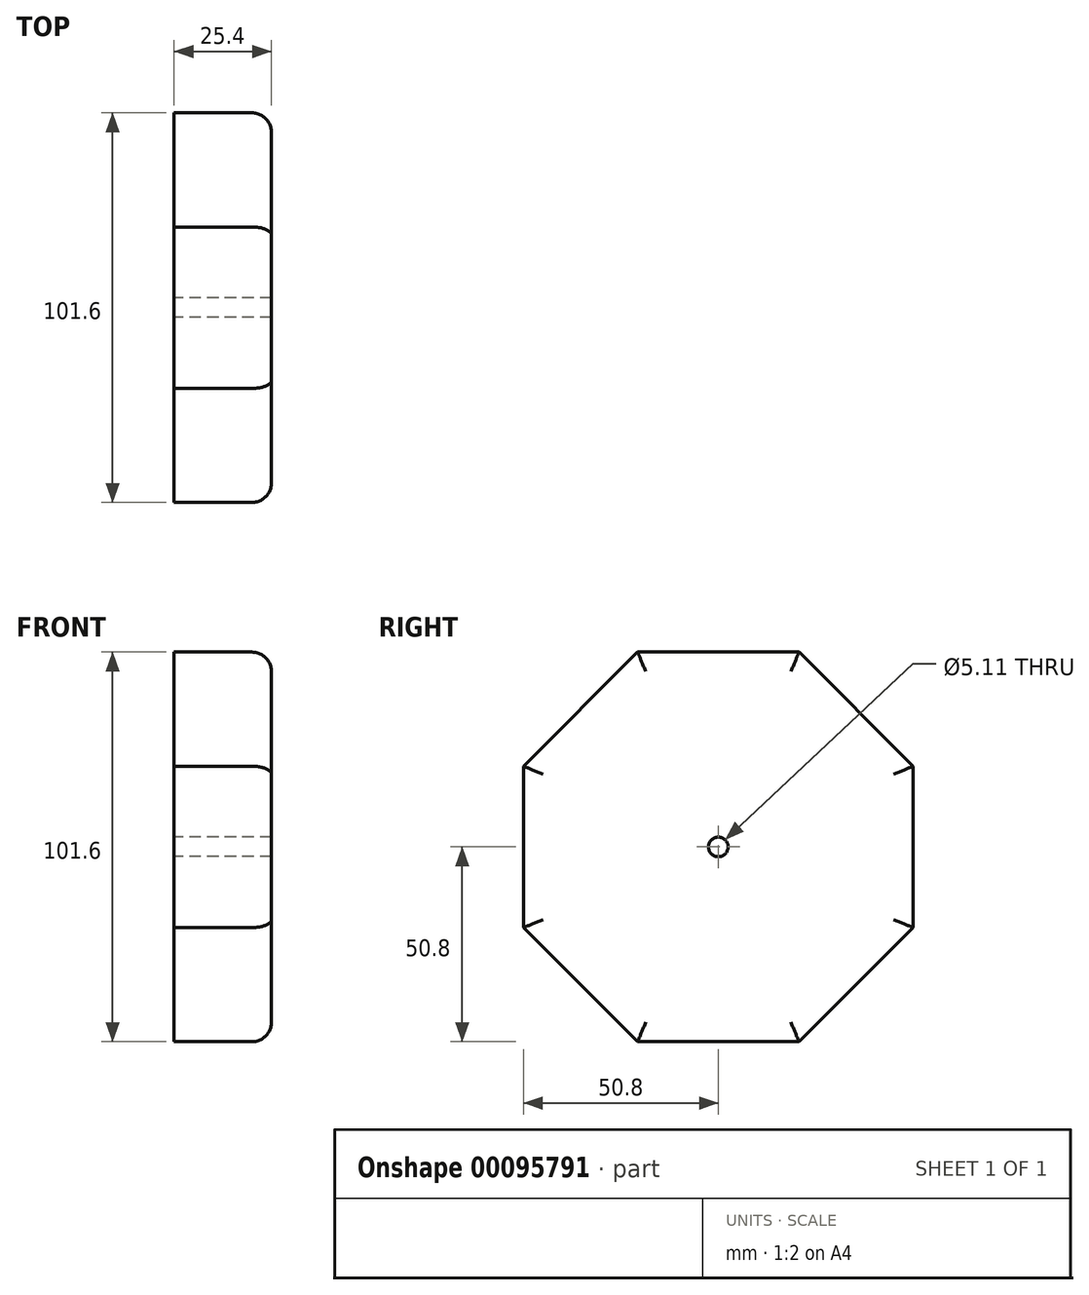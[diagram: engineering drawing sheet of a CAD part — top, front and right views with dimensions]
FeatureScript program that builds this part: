
annotation { "Feature Type Name" : "Feature", "Feature Type Description" : "" }
export const myFeature = defineFeature(function(context is Context, id is Id, definition is map)
    precondition{}
    {
        {
            var Q0;
            Q0=qCreatedBy(makeId("Right.planeOp"),FACE);
            var sketch = newSketch(context, id + "F0", { "sketchPlane" : qUnion([Q0])});
            skLineSegment(sketch, "E0.0", {"start": v(50.8, 21.04) * mm, "end": v(50.8, -21.04) * mm});
            skLineSegment(sketch, "E0.1", {"start": v(50.8, -21.04) * mm, "end": v(21.04, -50.8) * mm});
            skLineSegment(sketch, "E0.2", {"start": v(21.04, -50.8) * mm, "end": v(-21.04, -50.8) * mm});
            skLineSegment(sketch, "E0.3", {"start": v(-21.04, -50.8) * mm, "end": v(-50.8, -21.04) * mm});
            skLineSegment(sketch, "E0.4", {"start": v(-50.8, -21.04) * mm, "end": v(-50.8, 21.04) * mm});
            skLineSegment(sketch, "E0.5", {"start": v(-50.8, 21.04) * mm, "end": v(-21.04, 50.8) * mm});
            skLineSegment(sketch, "E0.6", {"start": v(-21.04, 50.8) * mm, "end": v(21.04, 50.8) * mm});
            skLineSegment(sketch, "E0.7", {"start": v(21.04, 50.8) * mm, "end": v(50.8, 21.04) * mm});
            skPoint(sketch, "E0.0.midPoint", {"position": v(50.8, 0) * mm});
            skPoint(sketch, "E1", {"position": v(0, 0) * mm});
            skSolve(sketch);
        }
        {
            var Q0;
            Q0 = qSketchRegion(id + "F0", true);
            extrude(context, id + "F1", {"entities" : qUnion([Q0]), "depth" : 25.4 * mm});
        }
        {
            var Q0;
            Q0=makeQuery(id+"F1.opExtrude","CAP_EDGE",EDGE,{"disambiguationData":[OSD([sQuery(id+"F0.wireOp",EDGE,"E0.5")])],"isStart":false});
            var Q1;
            Q1=makeQuery(id+"F1.opExtrude","CAP_EDGE",EDGE,{"disambiguationData":[OSD([sQuery(id+"F0.wireOp",EDGE,"E0.4")])],"isStart":false});
            var Q2;
            Q2=makeQuery(id+"F1.opExtrude","CAP_EDGE",EDGE,{"disambiguationData":[OSD([sQuery(id+"F0.wireOp",EDGE,"E0.3")])],"isStart":false});
            var Q3;
            Q3=makeQuery(id+"F1.opExtrude","CAP_EDGE",EDGE,{"disambiguationData":[OSD([sQuery(id+"F0.wireOp",EDGE,"E0.2")])],"isStart":false});
            var Q4;
            Q4=makeQuery(id+"F1.opExtrude","CAP_EDGE",EDGE,{"disambiguationData":[OSD([sQuery(id+"F0.wireOp",EDGE,"E0.1")])],"isStart":false});
            var Q5;
            Q5=makeQuery(id+"F1.opExtrude","CAP_EDGE",EDGE,{"disambiguationData":[OSD([sQuery(id+"F0.wireOp",EDGE,"E0.0")])],"isStart":false});
            var Q6;
            Q6=makeQuery(id+"F1.opExtrude","CAP_EDGE",EDGE,{"disambiguationData":[OSD([sQuery(id+"F0.wireOp",EDGE,"E0.7")])],"isStart":false});
            var Q7;
            Q7=makeQuery(id+"F1.opExtrude","CAP_EDGE",EDGE,{"disambiguationData":[OSD([sQuery(id+"F0.wireOp",EDGE,"E0.6")])],"isStart":false});
            fillet(context, id + "F2", {"entities" : qUnion([Q0, Q1, Q2, Q3, Q4, Q5, Q6, Q7]), "radius" : 5.08 * mm, "tangentPropagation" : true, "allowEdgeOverflow" : false});
        }
        {
            var Q0;
            Q0=sQuery(id+"F0.wireOp",VERTEX,"E1");
            var Q1;
            Q1=makeQuery(id+"F1.opExtrude","SWEPT_BODY",BODY,{"disambiguationData":[OSD([sQuery(id+"F0.wireOp",EDGE,"E0.0"),sQuery(id+"F0.wireOp",EDGE,"E0.1"),sQuery(id+"F0.wireOp",EDGE,"E0.2"),sQuery(id+"F0.wireOp",EDGE,"E0.3"),sQuery(id+"F0.wireOp",EDGE,"E0.4"),sQuery(id+"F0.wireOp",EDGE,"E0.5"),sQuery(id+"F0.wireOp",EDGE,"E0.6"),sQuery(id+"F0.wireOp",EDGE,"E0.7")])]});
            hole(context, id + "F3", {"style" : HoleStyle.SIMPLE, "endStyle" : HoleEndStyle.THROUGH, "oppositeDirection" : true, "standardTappedOrClearance" : lookupTablePath({ "standard" : "ANSI", "engagement" : "75%", "pitch" : "20 tpi", "size" : "1/4", "type" : "Tapped" }), "standardBlindInLast" : lookupTablePath({ "standard" : "ANSI", "engagement" : "75%", "pitch" : "20 tpi", "size" : "1/4", "type" : "Tapped" }), "holeDiameter" : 5.1 * mm, "locations" : qUnion([Q0]), "scope" : qUnion([Q1]), "isTappedThrough" : true, "majorDiameter" : 6.35 * mm, "showTappedDepth" : true});
        }
    });
